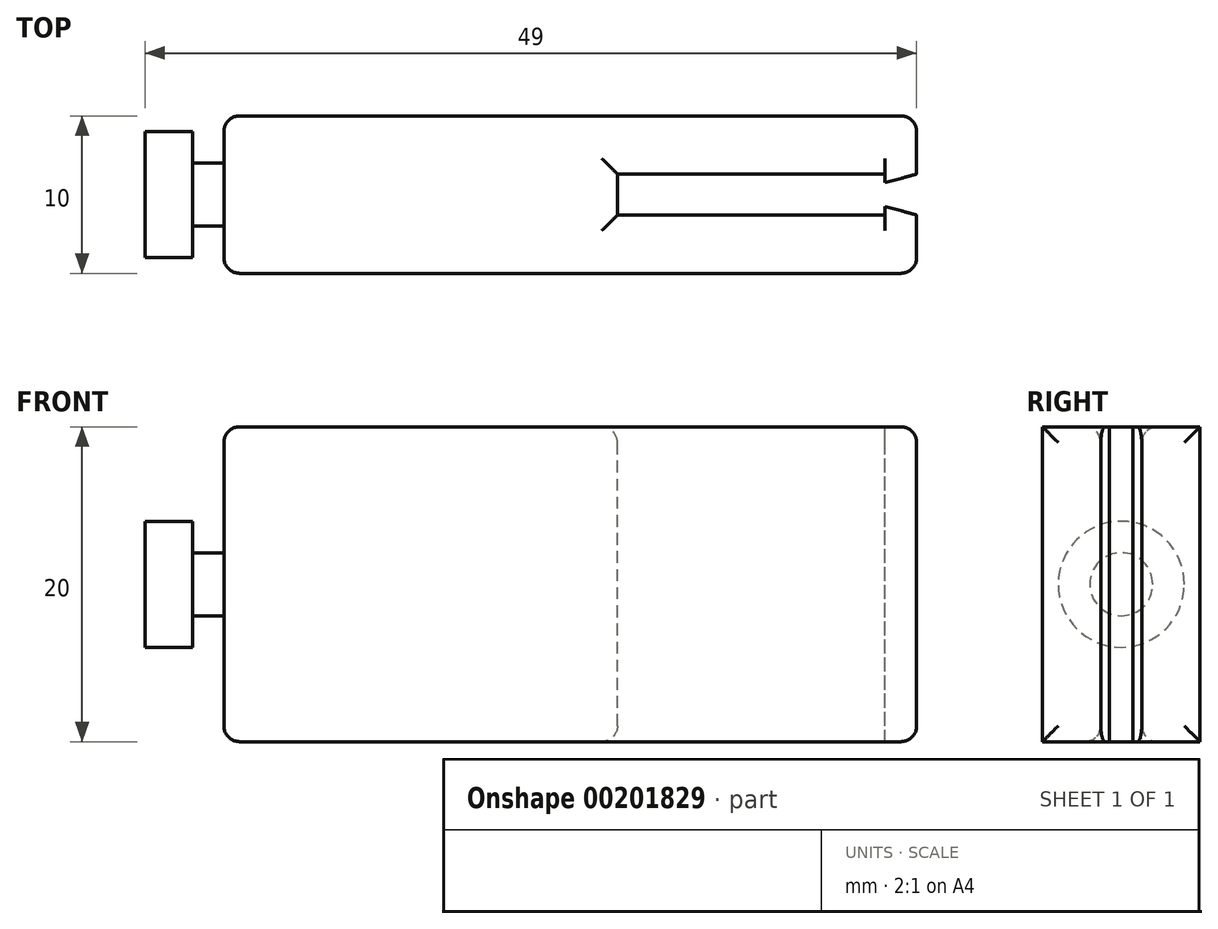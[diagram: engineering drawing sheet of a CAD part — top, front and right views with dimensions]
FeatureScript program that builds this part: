
annotation { "Feature Type Name" : "Feature", "Feature Type Description" : "" }
export const myFeature = defineFeature(function(context is Context, id is Id, definition is map)
    precondition{}
    {
        {
            var Q0;
            Q0=qCreatedBy(makeId("Front.planeOp"),FACE);
            var sketch = newSketch(context, id + "F0", { "sketchPlane" : qUnion([Q0])});
            skLineSegment(sketch, "E0.bottom", {"start": v(0, 0) * mm, "end": v(25, 0) * mm});
            skLineSegment(sketch, "E0.top", {"start": v(0, 5) * mm, "end": v(25, 5) * mm});
            skLineSegment(sketch, "E0.left", {"start": v(0, 0) * mm, "end": v(0, 5) * mm});
            skLineSegment(sketch, "E0.right", {"start": v(25, 0) * mm, "end": v(25, 5) * mm});
            skLineSegment(sketch, "E1.bottom", {"start": v(25, 5) * mm, "end": v(44, 5) * mm});
            skLineSegment(sketch, "E1.top", {"start": v(25, 1.3) * mm, "end": v(44, 1.3) * mm});
            skLineSegment(sketch, "E1.left", {"start": v(25, 5) * mm, "end": v(25, 1.3) * mm});
            skLineSegment(sketch, "E1.right", {"start": v(44, 5) * mm, "end": v(44, 1.3) * mm});
            skLineSegment(sketch, "E2.MirrorCS", {"start": v(0, 0) * mm, "end": v(0, -5) * mm});
            skLineSegment(sketch, "E3.MirrorCS", {"start": v(0, -5) * mm, "end": v(25, -5) * mm});
            skLineSegment(sketch, "E4.MirrorCS", {"start": v(25, -5) * mm, "end": v(44, -5) * mm});
            skLineSegment(sketch, "E5.MirrorCS", {"start": v(25, -1.3) * mm, "end": v(44, -1.3) * mm});
            skLineSegment(sketch, "E6.MirrorCS", {"start": v(25, 0) * mm, "end": v(25, -5) * mm});
            skLineSegment(sketch, "E7.MirrorCS", {"start": v(44, -5) * mm, "end": v(44, -1.3) * mm});
            skLineSegment(sketch, "E8", {"start": v(42, 1.3) * mm, "end": v(42, 0.75) * mm});
            skLineSegment(sketch, "E9", {"start": v(42, 0.75) * mm, "end": v(44, 1.3) * mm});
            skLineSegment(sketch, "E10.MirrorCS", {"start": v(42, -1.3) * mm, "end": v(42, -0.75) * mm});
            skLineSegment(sketch, "E11.MirrorCS", {"start": v(42, -0.75) * mm, "end": v(44, -1.3) * mm});
            skSolve(sketch);
        }
        {
            var Q0;
            Q0 = qSketchRegion(id + "F0", true);
            var Q1;
            Q1 = qSketchRegion(id + "F2", true);
            extrude(context, id + "F1", {"entities" : qUnion([Q0, Q1]), "endBound" : BoundingType.SYMMETRIC, "offsetDistance" : 25 * mm, "depth" : 20 * mm});
        }
        {
            var Q0;
            Q0=makeQuery(id+"F1.opExtrude","SWEPT_FACE",FACE,{"disambiguationData":[OSD([sQuery(id+"F0.wireOp",EDGE,"E0.left"),sQuery(id+"F0.wireOp",EDGE,"E2.MirrorCS")])]});
            var sketch = newSketch(context, id + "F2", { "sketchPlane" : qUnion([Q0])});
            skCircle(sketch, "E12", {"center": v(0, 0) * mm, "radius": 2 * mm});
            skSolve(sketch);
        }
        {
            var Q0;
            Q0=makeQuery(id+"F2.imprint","IMPRINT",FACE,{"disambiguationData":[TD([[makeQuery(id+"F2.imprint","IMPRINT",EDGE,{"derivedFrom":sQuery(id+"F2.wireOp",EDGE,"E12")}),1.0]])]});
            extrude(context, id + "F3", {"entities" : qUnion([Q0]), "operationType" : NewBodyOperationType.ADD, "depth" : 2 * mm});
        }
        {
            var Q0;
            Q0=makeQuery(id+"F3.opExtrude","CAP_FACE",FACE,{"disambiguationData":[OSD([sQuery(id+"F2.wireOp",EDGE,"E12")])],"isStart":false});
            var sketch = newSketch(context, id + "F4", { "sketchPlane" : qUnion([Q0])});
            skCircle(sketch, "E13", {"center": v(0, 0) * mm, "radius": 4 * mm});
            skSolve(sketch);
        }
        {
            var Q0;
            Q0=makeQuery(id+"F4.imprint","IMPRINT",FACE,{"disambiguationData":[TD([[makeQuery(id+"F4.imprint","IMPRINT",EDGE,{"derivedFrom":sQuery(id+"F4.wireOp",EDGE,"E13")}),1.0]])]});
            var Q1;
            Q1=makeQuery(id+"F4.imprint","IMPRINT",FACE,{"disambiguationData":[TD([[makeQuery(id+"F4.imprint","IMPRINT",EDGE,{"derivedFrom":makeQuery(id+"F3.opExtrude","CAP_EDGE",EDGE,{"disambiguationData":[OSD([sQuery(id+"F2.wireOp",EDGE,"E12")])],"isStart":false})}),1.0]])]});
            extrude(context, id + "F5", {"entities" : qUnion([Q0, Q1]), "operationType" : NewBodyOperationType.ADD, "depth" : 3 * mm});
        }
        {
            var Q0;
            Q0=makeQuery(id+"F1.opExtrude","CAP_EDGE",EDGE,{"disambiguationData":[OSD([sQuery(id+"F0.wireOp",EDGE,"E1.right")])],"isStart":false});
            var Q1;
            Q1=makeQuery(id+"F1.opExtrude","CAP_EDGE",EDGE,{"disambiguationData":[OSD([sQuery(id+"F0.wireOp",EDGE,"E1.right")])],"isStart":true});
            var Q2;
            Q2=makeQuery(id+"F1.opExtrude","CAP_EDGE",EDGE,{"disambiguationData":[OSD([sQuery(id+"F0.wireOp",EDGE,"E7.MirrorCS")])],"isStart":true});
            var Q3;
            Q3=makeQuery(id+"F1.opExtrude","CAP_EDGE",EDGE,{"disambiguationData":[OSD([sQuery(id+"F0.wireOp",EDGE,"E7.MirrorCS")])],"isStart":false});
            var Q4;
            Q4=makeQuery(id+"F1.opExtrude","CAP_EDGE",EDGE,{"disambiguationData":[OSD([sQuery(id+"F0.wireOp",EDGE,"E0.left"),sQuery(id+"F0.wireOp",EDGE,"E2.MirrorCS")])],"isStart":false});
            var Q5;
            Q5=makeQuery(id+"F1.opExtrude","CAP_EDGE",EDGE,{"disambiguationData":[OSD([sQuery(id+"F0.wireOp",EDGE,"E0.left"),sQuery(id+"F0.wireOp",EDGE,"E2.MirrorCS")])],"isStart":true});
            var Q6;
            Q6=makeQuery(id+"F1.opExtrude","SWEPT_EDGE",EDGE,{"disambiguationData":[OSD([sQuery(id+"F0.wireOp",EDGE,"E0.top"),sQuery(id+"F0.wireOp",EDGE,"E0.left")])]});
            var Q7;
            Q7=makeQuery(id+"F1.opExtrude","SWEPT_EDGE",EDGE,{"disambiguationData":[OSD([sQuery(id+"F0.wireOp",EDGE,"E2.MirrorCS"),sQuery(id+"F0.wireOp",EDGE,"E3.MirrorCS")])]});
            var Q8;
            Q8=makeQuery(id+"F1.opExtrude","SWEPT_EDGE",EDGE,{"disambiguationData":[OSD([sQuery(id+"F0.wireOp",EDGE,"E4.MirrorCS"),sQuery(id+"F0.wireOp",EDGE,"E7.MirrorCS")])]});
            var Q9;
            Q9=makeQuery(id+"F1.opExtrude","SWEPT_EDGE",EDGE,{"disambiguationData":[OSD([sQuery(id+"F0.wireOp",EDGE,"E1.bottom"),sQuery(id+"F0.wireOp",EDGE,"E1.right")])]});
            var Q10;
            Q10=makeQuery(id+"F1.opExtrude","CAP_EDGE",EDGE,{"disambiguationData":[OSD([sQuery(id+"F0.wireOp",EDGE,"E1.top")])],"isStart":false});
            var Q11;
            Q11=makeQuery(id+"F1.opExtrude","CAP_EDGE",EDGE,{"disambiguationData":[OSD([sQuery(id+"F0.wireOp",EDGE,"E5.MirrorCS")])],"isStart":false});
            var Q12;
            Q12=makeQuery(id+"F1.opExtrude","CAP_EDGE",EDGE,{"disambiguationData":[OSD([sQuery(id+"F0.wireOp",EDGE,"E0.right"),sQuery(id+"F0.wireOp",EDGE,"E6.MirrorCS")])],"isStart":false});
            var Q13;
            Q13=makeQuery(id+"F1.opExtrude","CAP_EDGE",EDGE,{"disambiguationData":[OSD([sQuery(id+"F0.wireOp",EDGE,"E0.right"),sQuery(id+"F0.wireOp",EDGE,"E6.MirrorCS")])],"isStart":true});
            var Q14;
            Q14=makeQuery(id+"F1.opExtrude","CAP_EDGE",EDGE,{"disambiguationData":[OSD([sQuery(id+"F0.wireOp",EDGE,"E1.top")])],"isStart":true});
            var Q15;
            Q15=makeQuery(id+"F1.opExtrude","CAP_EDGE",EDGE,{"disambiguationData":[OSD([sQuery(id+"F0.wireOp",EDGE,"E5.MirrorCS")])],"isStart":true});
            fillet(context, id + "F6", {"entities" : qUnion([Q0, Q1, Q2, Q3, Q4, Q5, Q6, Q7, Q8, Q9, Q10, Q11, Q12, Q13, Q14, Q15]), "radius" : 1 * mm, "tangentPropagation" : true, "allowEdgeOverflow" : false});
        }
        {
            var Q0;
            Q0=makeQuery(id+"F1.opExtrude","SWEPT_BODY",BODY,{"disambiguationData":[OSD([sQuery(id+"F0.wireOp",EDGE,"E0.top"),sQuery(id+"F0.wireOp",EDGE,"E0.left"),sQuery(id+"F0.wireOp",EDGE,"E0.right"),sQuery(id+"F0.wireOp",EDGE,"E1.bottom"),sQuery(id+"F0.wireOp",EDGE,"E1.top"),sQuery(id+"F0.wireOp",EDGE,"E2.MirrorCS"),sQuery(id+"F0.wireOp",EDGE,"E3.MirrorCS"),sQuery(id+"F0.wireOp",EDGE,"E4.MirrorCS"),sQuery(id+"F0.wireOp",EDGE,"E5.MirrorCS"),sQuery(id+"F0.wireOp",EDGE,"E6.MirrorCS"),sQuery(id+"F0.wireOp",EDGE,"NKTIYT2v-Aoue-tqdF-kBF8-sw4m7ksejeBJ.bottom"),sQuery(id+"F0.wireOp",EDGE,"NKTIYT2v-Aoue-tqdF-kBF8-sw4m7ksejeBJ.top"),sQuery(id+"F0.wireOp",EDGE,"NKTIYT2v-Aoue-tqdF-kBF8-sw4m7ksejeBJ.left"),sQuery(id+"F0.wireOp",EDGE,"NKTIYT2v-Aoue-tqdF-kBF8-sw4m7ksejeBJ.right"),sQuery(id+"F0.wireOp",EDGE,"90b3f183-4c8a-4fe5-b47e-5de90468e0930.MirrorCS"),sQuery(id+"F0.wireOp",EDGE,"268f5e7c-e49a-4d73-82eb-b18f2ec75a5a0.MirrorCS"),sQuery(id+"F0.wireOp",EDGE,"3c9f35ad-dd32-44b7-b06f-76abd0e59cc70.MirrorCS"),sQuery(id+"F0.wireOp",EDGE,"772d3055-bd9f-4468-86a3-08712100c5180.MirrorCS")])]});
            var Q1;
            Q1=sQuery(id+"F0.wireOp",EDGE,"E0.bottom");
            transform(context, id + "F7", {"entities" : qUnion([Q0]), "transformType" : TransformType.ROTATION, "transformAxis" : qUnion([Q1]), "angle" : 90 * degree, "makeCopy" : false});
        }
    });
